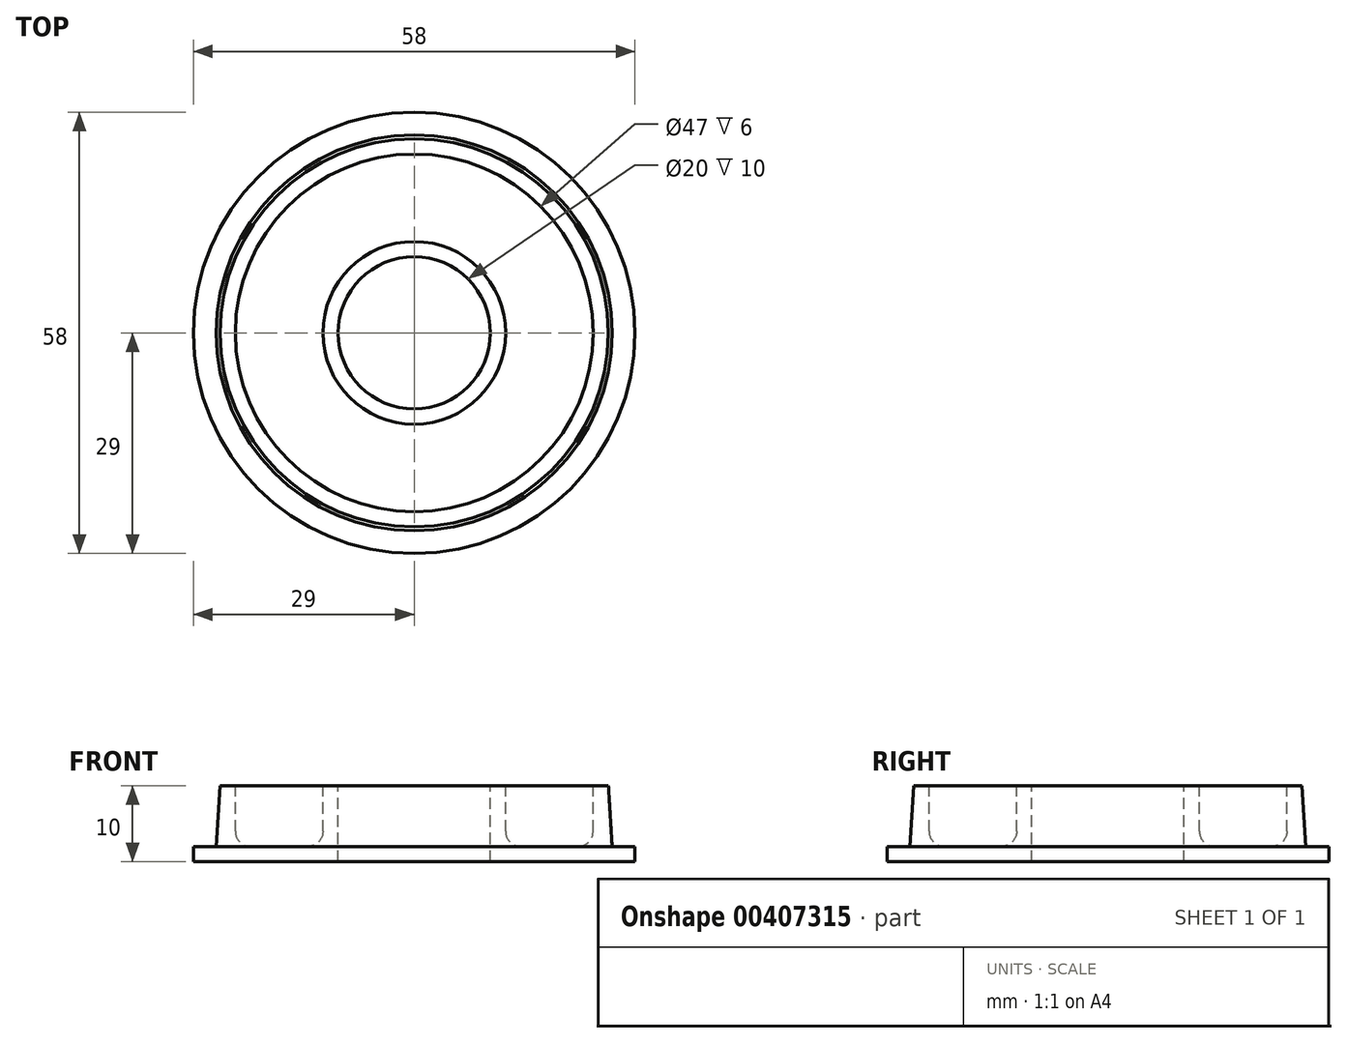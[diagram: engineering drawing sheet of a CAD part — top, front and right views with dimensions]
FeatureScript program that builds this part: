
annotation { "Feature Type Name" : "Feature", "Feature Type Description" : "" }
export const myFeature = defineFeature(function(context is Context, id is Id, definition is map)
    precondition{}
    {
        {
            var Q0;
            Q0=qCreatedBy(makeId("Front.planeOp"),FACE);
            var sketch = newSketch(context, id + "F0", { "sketchPlane" : qUnion([Q0])});
            skLineSegment(sketch, "E0", {"start": v(10, 10) * mm, "end": v(10, 0) * mm});
            skLineSegment(sketch, "E1", {"start": v(10, 0) * mm, "end": v(29, 0) * mm});
            skLineSegment(sketch, "E2", {"start": v(29, 0) * mm, "end": v(29, 2) * mm});
            skLineSegment(sketch, "E3", {"start": v(29, 2) * mm, "end": v(26, 2) * mm});
            skLineSegment(sketch, "E4", {"start": v(26, 2) * mm, "end": v(25.5, 10) * mm});
            skLineSegment(sketch, "E5", {"start": v(25.5, 10) * mm, "end": v(23.5, 10) * mm});
            skLineSegment(sketch, "E6", {"start": v(0, 10) * mm, "end": v(0, 10) * mm});
            skLineSegment(sketch, "E7", {"start": v(0, 36.4) * mm, "end": v(0, 10) * mm, "construction": true});
            skLineSegment(sketch, "E8", {"start": v(10, 10) * mm, "end": v(10, 10) * mm});
            skLineSegment(sketch, "E9.trimOffspring", {"start": v(0, 10) * mm, "end": v(0, -40.6) * mm, "construction": true});
            skLineSegment(sketch, "E10", {"start": v(12, 10) * mm, "end": v(12, 2) * mm});
            skLineSegment(sketch, "E11", {"start": v(12, 2) * mm, "end": v(23.5, 2) * mm});
            skLineSegment(sketch, "E12", {"start": v(23.5, 2) * mm, "end": v(23.5, 10) * mm});
            skLineSegment(sketch, "E13.trimOffspring", {"start": v(12, 10) * mm, "end": v(10, 10) * mm});
            skSolve(sketch);
        }
        {
            var Q0;
            Q0 = qSketchRegion(id + "F0", true);
            var Q1;
            Q1=sQuery(id+"F0.wireOp",EDGE,"E7");
            revolve(context, id + "F1", {"entities" : qUnion([Q0]), "axis" : qUnion([Q1]), "revolveType" : RevolveType.FULL});
        }
        {
            var Q0;
            Q0=makeQuery(id+"F1.opRevolve","SWEPT_EDGE",EDGE,{"disambiguationData":[OSD([sQuery(id+"F0.wireOp",EDGE,"E10"),sQuery(id+"F0.wireOp",EDGE,"E11")])]});
            var Q1;
            Q1=makeQuery(id+"F1.opRevolve","SWEPT_EDGE",EDGE,{"disambiguationData":[OSD([sQuery(id+"F0.wireOp",EDGE,"E11"),sQuery(id+"F0.wireOp",EDGE,"E12")])]});
            fillet(context, id + "F2", {"entities" : qUnion([Q0, Q1]), "radius" : 2 * mm, "tangentPropagation" : true, "allowEdgeOverflow" : false});
        }
    });
